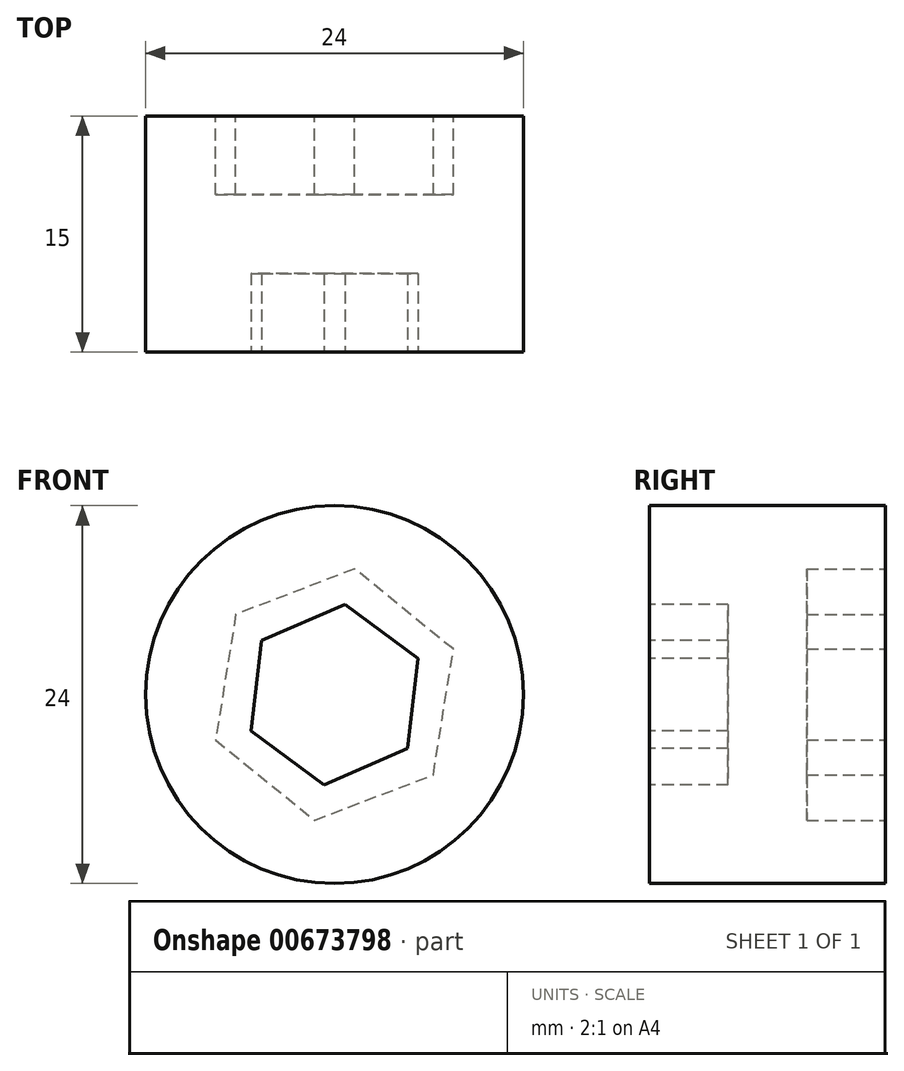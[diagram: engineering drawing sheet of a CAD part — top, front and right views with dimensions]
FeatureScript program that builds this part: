
annotation { "Feature Type Name" : "Feature", "Feature Type Description" : "" }
export const myFeature = defineFeature(function(context is Context, id is Id, definition is map)
    precondition{}
    {
        {
            var Q0;
            Q0=qCreatedBy(makeId("Front.planeOp"),FACE);
            var sketch = newSketch(context, id + "F0", { "sketchPlane" : qUnion([Q0])});
            skCircle(sketch, "E0", {"center": v(0, 0) * mm, "radius": 12 * mm});
            skSolve(sketch);
        }
        {
            var Q0;
            Q0=makeQuery(id+"F0.imprint","IMPRINT",FACE,{"disambiguationData":[TD([[makeQuery(id+"F0.imprint","IMPRINT",EDGE,{"derivedFrom":sQuery(id+"F0.wireOp",EDGE,"E0")}),1.0]])]});
            extrude(context, id + "F1", {"entities" : qUnion([Q0]), "depth" : 15 * mm, "offsetDistance" : 25 * mm});
        }
        {
            var Q0;
            Q0=makeQuery(id+"F1.opExtrude","CAP_FACE",FACE,{"disambiguationData":[OSD([sQuery(id+"F0.wireOp",EDGE,"E0")])],"isStart":false});
            var sketch = newSketch(context, id + "F2", { "sketchPlane" : qUnion([Q0])});
            skCircle(sketch, "E1.cCircle", {"center": v(0, 0) * mm, "radius": 5 * mm, "construction": true});
            skLineSegment(sketch, "E1.0", {"start": v(0.65, 5.74) * mm, "end": v(5.3, 2.3) * mm});
            skLineSegment(sketch, "E1.1", {"start": v(5.3, 2.3) * mm, "end": v(4.64, -3.43) * mm});
            skLineSegment(sketch, "E1.2", {"start": v(4.64, -3.43) * mm, "end": v(-0.65, -5.74) * mm});
            skLineSegment(sketch, "E1.3", {"start": v(-0.65, -5.74) * mm, "end": v(-5.3, -2.3) * mm});
            skLineSegment(sketch, "E1.4", {"start": v(-5.3, -2.3) * mm, "end": v(-4.64, 3.43) * mm});
            skLineSegment(sketch, "E1.5", {"start": v(-4.64, 3.43) * mm, "end": v(0.65, 5.74) * mm});
            skPoint(sketch, "E1.0.midPoint", {"position": v(2.97, 4.02) * mm});
            skSolve(sketch);
        }
        {
            var Q0;
            Q0=makeQuery(id+"F2.imprint","IMPRINT",FACE,{"disambiguationData":[TD([[makeQuery(id+"F2.imprint","IMPRINT",EDGE,{"derivedFrom":sQuery(id+"F2.wireOp",EDGE,"E1.0")}),-1.0]])]});
            extrude(context, id + "F3", {"entities" : qUnion([Q0]), "operationType" : NewBodyOperationType.REMOVE, "oppositeDirection" : true, "depth" : 5 * mm, "offsetDistance" : 25 * mm});
        }
        {
            var Q0;
            Q0=makeQuery(id+"F1.opExtrude","CAP_FACE",FACE,{"disambiguationData":[OSD([sQuery(id+"F0.wireOp",EDGE,"E0")])],"isStart":true});
            var sketch = newSketch(context, id + "F4", { "sketchPlane" : qUnion([Q0])});
            skCircle(sketch, "E2.cCircle", {"center": v(0, 0) * mm, "radius": 7 * mm, "construction": true});
            skLineSegment(sketch, "E2.0", {"start": v(-1.28, 7.98) * mm, "end": v(6.27, 5.1) * mm});
            skLineSegment(sketch, "E2.1", {"start": v(6.27, 5.1) * mm, "end": v(7.55, -2.89) * mm});
            skLineSegment(sketch, "E2.2", {"start": v(7.55, -2.89) * mm, "end": v(1.28, -7.98) * mm});
            skLineSegment(sketch, "E2.3", {"start": v(1.28, -7.98) * mm, "end": v(-6.27, -5.1) * mm});
            skLineSegment(sketch, "E2.4", {"start": v(-6.27, -5.1) * mm, "end": v(-7.55, 2.89) * mm});
            skLineSegment(sketch, "E2.5", {"start": v(-7.55, 2.89) * mm, "end": v(-1.28, 7.98) * mm});
            skPoint(sketch, "E2.0.midPoint", {"position": v(2.5, 6.54) * mm});
            skSolve(sketch);
        }
        {
            var Q0;
            Q0=makeQuery(id+"F4.imprint","IMPRINT",FACE,{"disambiguationData":[TD([[makeQuery(id+"F4.imprint","IMPRINT",EDGE,{"derivedFrom":sQuery(id+"F4.wireOp",EDGE,"E2.0")}),-1.0]])]});
            extrude(context, id + "F5", {"entities" : qUnion([Q0]), "operationType" : NewBodyOperationType.REMOVE, "oppositeDirection" : true, "depth" : 5 * mm, "offsetDistance" : 25 * mm});
        }
    });
